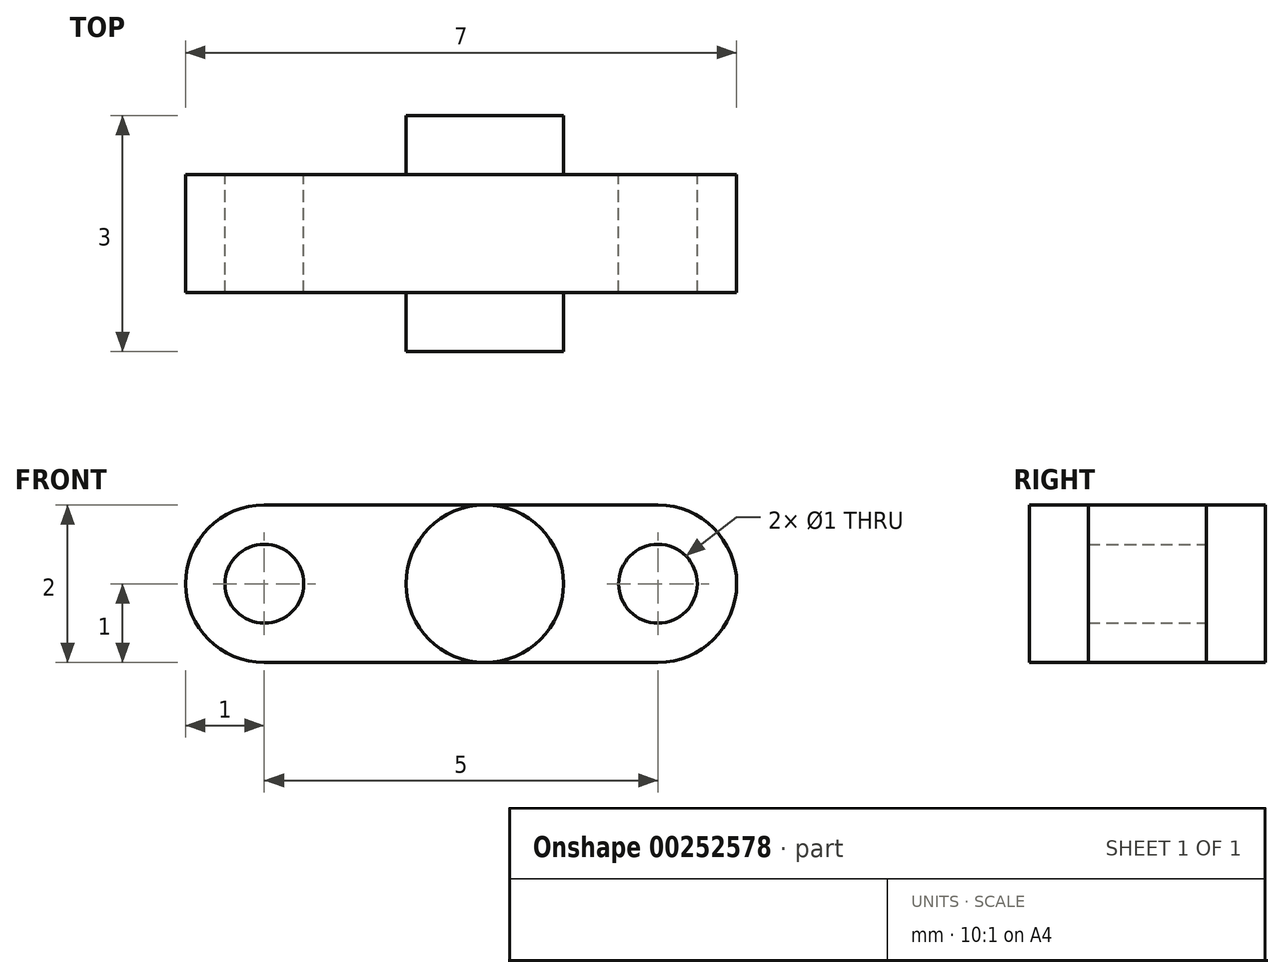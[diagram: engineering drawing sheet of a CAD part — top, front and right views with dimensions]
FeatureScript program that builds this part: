
annotation { "Feature Type Name" : "Feature", "Feature Type Description" : "" }
export const myFeature = defineFeature(function(context is Context, id is Id, definition is map)
    precondition{}
    {
        {
            var Q0;
            Q0=qCreatedBy(makeId("Front.planeOp"),FACE);
            var sketch = newSketch(context, id + "F0", { "sketchPlane" : qUnion([Q0])});
            skLineSegment(sketch, "E0.bottom", {"start": v(-2.2, -0.2) * mm, "end": v(-5, -0.2) * mm});
            skLineSegment(sketch, "E0.top", {"start": v(-2.2, -2.2) * mm, "end": v(-5, -2.2) * mm});
            skArc(sketch, "E1", {"start": v(0, -2.2) * mm, "mid": v(1, -1.2) * mm, "end": v(0, -0.2) * mm});
            skLineSegment(sketch, "E2", {"start": v(-2.2, -0.2) * mm, "end": v(0, -0.2) * mm});
            skLineSegment(sketch, "E3", {"start": v(-2.2, -2.2) * mm, "end": v(0, -2.2) * mm});
            skArc(sketch, "E4", {"start": v(-2.8, -0.2) * mm, "mid": v(-3.8, -1.2) * mm, "end": v(-2.8, -2.2) * mm});
            skPoint(sketch, "E5", {"position": v(-5, -1.2) * mm});
            skCircle(sketch, "E6", {"center": v(-5, -1.2) * mm, "radius": 0.5 * mm});
            skCircle(sketch, "E7", {"center": v(0, -1.2) * mm, "radius": 0.5 * mm});
            skArc(sketch, "E8", {"start": v(-2.2, -2.2) * mm, "mid": v(-1.2, -1.2) * mm, "end": v(-2.2, -0.2) * mm});
            skLineSegment(sketch, "E9", {"start": v(-5, -0.2) * mm, "end": v(-5, -0.2) * mm});
            skArc(sketch, "E10", {"start": v(-5, -0.2) * mm, "mid": v(-6, -1.2) * mm, "end": v(-5, -2.2) * mm});
            skLineSegment(sketch, "E11", {"start": v(-6, -1.2) * mm, "end": v(1, -1.2) * mm, "construction": true});
            skCircle(sketch, "E12", {"center": v(-2.2, -1.2) * mm, "radius": 1 * mm});
            skSolve(sketch);
        }
        {
            var Q0;
            {var subQ5=sQuery(id+"F0.wireOp",EDGE,"E4");Q0=makeQuery(id+"F0.imprint","IMPRINT",FACE,{"disambiguationData":[TD([[makeQuery(id+"F0.imprint","IMPRINT",EDGE,{"derivedFrom":subQ5}),1.0]])]});}
            var Q1;
            Q1=makeQuery(id+"F0.imprint","IMPRINT",FACE,{"disambiguationData":[TD([[makeQuery(id+"F0.imprint","IMPRINT",EDGE,{"derivedFrom":sQuery(id+"F0.wireOp",EDGE,"E1")}),1.0]])]});
            var Q2;
            {var subQ0=sQuery(id+"F0.wireOp",EDGE,"bQbziyav-jX1J-XLfE-gFu1-S9SHtQTFnJFi");var subQ1=sQuery(id+"F0.wireOp",EDGE,"Mre1yFln-Q6Go-vBB8-nmWn-4SXoC3vIunpy");var subQ2=makeQuery(id+"F0.imprint","INTERSECT",VERTEX,{"derivedFrom":[subQ1,subQ0]});Q2=makeQuery(id+"F0.imprint","IMPRINT",FACE,{"disambiguationData":[TD([[makeQuery(id+"F0.imprint","IMPRINT",EDGE,{"disambiguationData":[TD([[subQ2,1.0]])],"derivedFrom":subQ1}),1.0]])]});}
            var Q3;
            {var subQ1=sQuery(id+"F0.wireOp",EDGE,"E0.bottom");var subQ3=sQuery(id+"F0.wireOp",EDGE,"Mre1yFln-Q6Go-vBB8-nmWn-4SXoC3vIunpy");var subQ4=makeQuery(id+"F0.imprint","INTERSECT",VERTEX,{"derivedFrom":[subQ1,subQ3]});Q3=makeQuery(id+"F0.imprint","IMPRINT",FACE,{"disambiguationData":[TD([[makeQuery(id+"F0.imprint","IMPRINT",EDGE,{"disambiguationData":[TD([[subQ4,-1.0]])],"derivedFrom":subQ3}),1.0]])]});}
            var Q4;
            {var subQ1=sQuery(id+"F0.wireOp",EDGE,"E0.top");var subQ3=sQuery(id+"F0.wireOp",EDGE,"bQbziyav-jX1J-XLfE-gFu1-S9SHtQTFnJFi");var subQ4=makeQuery(id+"F0.imprint","INTERSECT",VERTEX,{"derivedFrom":[subQ1,subQ3]});Q4=makeQuery(id+"F0.imprint","IMPRINT",FACE,{"disambiguationData":[TD([[makeQuery(id+"F0.imprint","IMPRINT",EDGE,{"disambiguationData":[TD([[subQ4,1.0]])],"derivedFrom":subQ3}),1.0]])]});}
            var Q5;
            {var subQ0=sQuery(id+"F0.wireOp",EDGE,"E4");Q5=makeQuery(id+"F0.imprint","IMPRINT",FACE,{"disambiguationData":[TD([[makeQuery(id+"F0.imprint","IMPRINT",EDGE,{"derivedFrom":subQ0}),-1.0]])]});}
            var Q6;
            {var subQ1=sQuery(id+"F0.wireOp",EDGE,"E0.bottom");var subQ3=sQuery(id+"F0.wireOp",EDGE,"E8");var subQ4=makeQuery(id+"F0.imprint","INTERSECT",VERTEX,{"derivedFrom":[subQ1,subQ3]});Q6=makeQuery(id+"F0.imprint","IMPRINT",FACE,{"disambiguationData":[TD([[makeQuery(id+"F0.imprint","IMPRINT",EDGE,{"disambiguationData":[TD([[subQ4,1.0]])],"derivedFrom":subQ3}),-1.0]])]});}
            var Q7;
            {var subQ1=sQuery(id+"F0.wireOp",EDGE,"E0.top");var subQ3=sQuery(id+"F0.wireOp",EDGE,"E8");var subQ4=makeQuery(id+"F0.imprint","INTERSECT",VERTEX,{"derivedFrom":[subQ1,subQ3]});Q7=makeQuery(id+"F0.imprint","IMPRINT",FACE,{"disambiguationData":[TD([[makeQuery(id+"F0.imprint","IMPRINT",EDGE,{"disambiguationData":[TD([[subQ4,-1.0]])],"derivedFrom":subQ3}),-1.0]])]});}
            var Q8;
            {var subQ0=sQuery(id+"F0.wireOp",EDGE,"E8");Q8=makeQuery(id+"F0.imprint","IMPRINT",FACE,{"disambiguationData":[TD([[makeQuery(id+"F0.imprint","IMPRINT",EDGE,{"derivedFrom":subQ0}),1.0]])]});}
            var Q9;
            {var subQ0=sQuery(id+"F0.wireOp",EDGE,"E12");var subQ1=makeQuery(id+"F0.imprint","INTERSECT",VERTEX,{"derivedFrom":[sQuery(id+"F0.wireOp",EDGE,"E0.bottom"),sQuery(id+"F0.wireOp",EDGE,"E2"),subQ0]});Q9=makeQuery(id+"F0.imprint","IMPRINT",FACE,{"disambiguationData":[TD([[makeQuery(id+"F0.imprint","IMPRINT",EDGE,{"disambiguationData":[TD([[subQ1,-1.0]])],"derivedFrom":subQ0}),1.0]])]});}
            extrude(context, id + "F1", {"entities" : qUnion([Q0, Q1, Q2, Q3, Q4, Q5, Q6, Q7, Q8, Q9]), "depth" : 1.5 * mm});
        }
        {
            var Q0;
            {var subQ0=sQuery(id+"F0.wireOp",EDGE,"E12");var subQ1=makeQuery(id+"F0.imprint","INTERSECT",VERTEX,{"derivedFrom":[sQuery(id+"F0.wireOp",EDGE,"E0.bottom"),sQuery(id+"F0.wireOp",EDGE,"E2"),subQ0]});Q0=makeQuery(id+"F0.imprint","IMPRINT",FACE,{"disambiguationData":[TD([[makeQuery(id+"F0.imprint","IMPRINT",EDGE,{"disambiguationData":[TD([[subQ1,-1.0]])],"derivedFrom":subQ0}),1.0]])]});}
            extrude(context, id + "F2", {"entities" : qUnion([Q0]), "operationType" : NewBodyOperationType.ADD, "oppositeDirection" : true, "depth" : 0.75 * mm, "hasSecondDirection" : true, "secondDirectionOppositeDirection" : false, "secondDirectionDepth" : 2.25 * mm});
        }
    });
